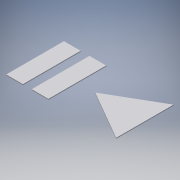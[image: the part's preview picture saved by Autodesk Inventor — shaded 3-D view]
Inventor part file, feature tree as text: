
AUTODESK INVENTOR PART (.ipt)
format: ipt  version: 2018 (Build 220112000, 112)  size: 114,688 bytes
history: native  units: mm
features: other x3, extrude x1, sketch x1, reference x1
ambient origin geometry x8: Origin, YZ Plane, XZ Plane, XY Plane, X Axis, Y Axis, Z Axis, Center Point
bodies: Volumenkörper1 (feature_tree)
feature tree (6):
  extrude  "Extrusion1"  Depth=0.2mm
  sketch  "Skizze1"  dims[d0=0.05mm d1=0.05mm d2=0.05mm d3=0.2mm d4=0.0mm]
  reference  "Referenz1"
  parser-record x1  (decoder bookkeeping rows leaked as tree rows — omitted from the tree; the rows remain in map.json)
  other  "VolumeKnob.iam"
  other  "Drehregler:1"
note: 1 file-system path scrubbed to <path> (originals preserved in map.json)
